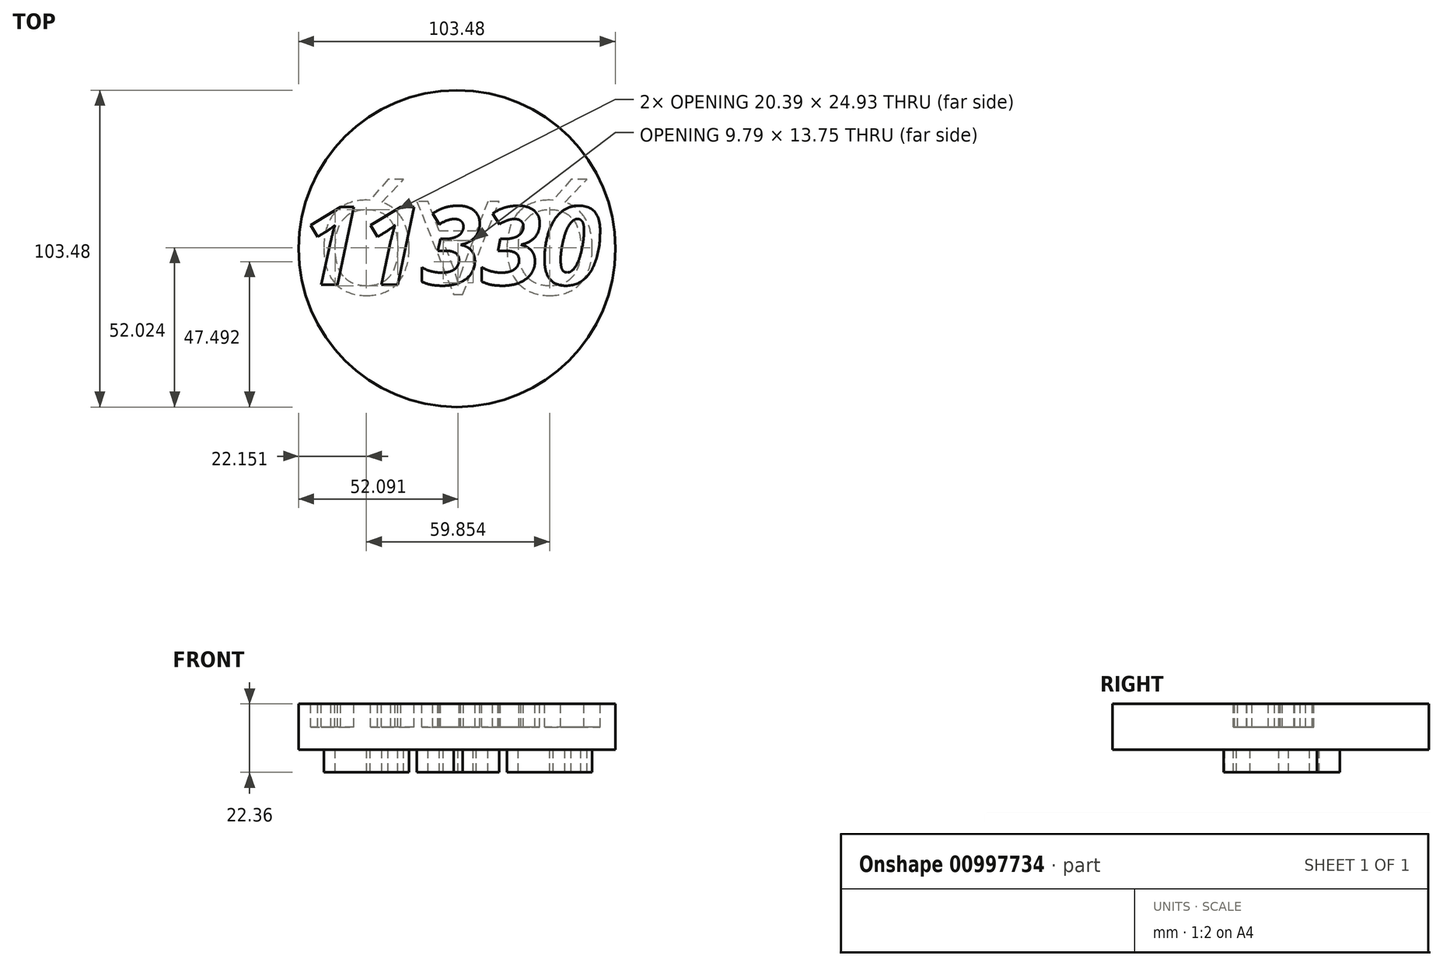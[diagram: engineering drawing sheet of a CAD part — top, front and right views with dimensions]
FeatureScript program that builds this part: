
annotation { "Feature Type Name" : "Feature", "Feature Type Description" : "" }
export const myFeature = defineFeature(function(context is Context, id is Id, definition is map)
    precondition{}
    {
        {
            var Q0;
            Q0=qCreatedBy(makeId("Top.planeOp"),FACE);
            var sketch = newSketch(context, id + "F0", { "sketchPlane" : qUnion([Q0])});
            skCircle(sketch, "E0", {"center": v(0, 0) * mm, "radius": 51.74 * mm});
            skSolve(sketch);
        }
        {
            var Q0;
            Q0=makeQuery(id+"F0.imprint","IMPRINT",FACE,{"disambiguationData":[TD([[makeQuery(id+"F0.imprint","IMPRINT",EDGE,{"derivedFrom":sQuery(id+"F0.wireOp",EDGE,"E0")}),1.0]])]});
            extrude(context, id + "F1", {"entities" : qUnion([Q0]), "depth" : 15 * mm, "offsetDistance" : 25.4 * mm});
        }
        {
            var Q0;
            Q0=makeQuery(id+"F1.opExtrude","CAP_FACE",FACE,{"disambiguationData":[OSD([sQuery(id+"F0.wireOp",EDGE,"E0")])],"isStart":false});
            var sketch = newSketch(context, id + "F2", { "sketchPlane" : qUnion([Q0])});
            skText(sketch, "E1", { "text": "11330", "fontName": "OpenSans-BoldItalic.ttf"});
            const initialGuessF2  = {"E1": [-0.051, -0.01178, 1, 0, 0.02564]};
            skSetInitialGuess(sketch, initialGuessF2);
            skSolve(sketch);
        }
        {
            var Q0;
            Q0 = qSketchRegion(id + "F2", true);
            extrude(context, id + "F3", {"entities" : qUnion([Q0]), "operationType" : NewBodyOperationType.REMOVE, "oppositeDirection" : true, "depth" : 7.62 * mm, "offsetDistance" : 25.4 * mm});
        }
        {
            var Q0;
            Q0=makeQuery(id+"F1.opExtrude","CAP_FACE",FACE,{"disambiguationData":[OSD([sQuery(id+"F0.wireOp",EDGE,"E0")])],"isStart":true});
            var sketch = newSketch(context, id + "F4", { "sketchPlane" : qUnion([Q0])});
            skText(sketch, "E2", { "text": "QAQ\n", "fontName": "OpenSans-Regular.ttf"});
            const initialGuessF4  = {"E2": [-0.0461, -0.01542, 1, 0, 0.03053]};
            skSetInitialGuess(sketch, initialGuessF4);
            skSolve(sketch);
        }
        {
            var Q0;
            Q0 = qSketchRegion(id + "F4", true);
            extrude(context, id + "F5", {"entities" : qUnion([Q0]), "depth" : 7.37 * mm, "offsetDistance" : 25.4 * mm});
        }
    });
